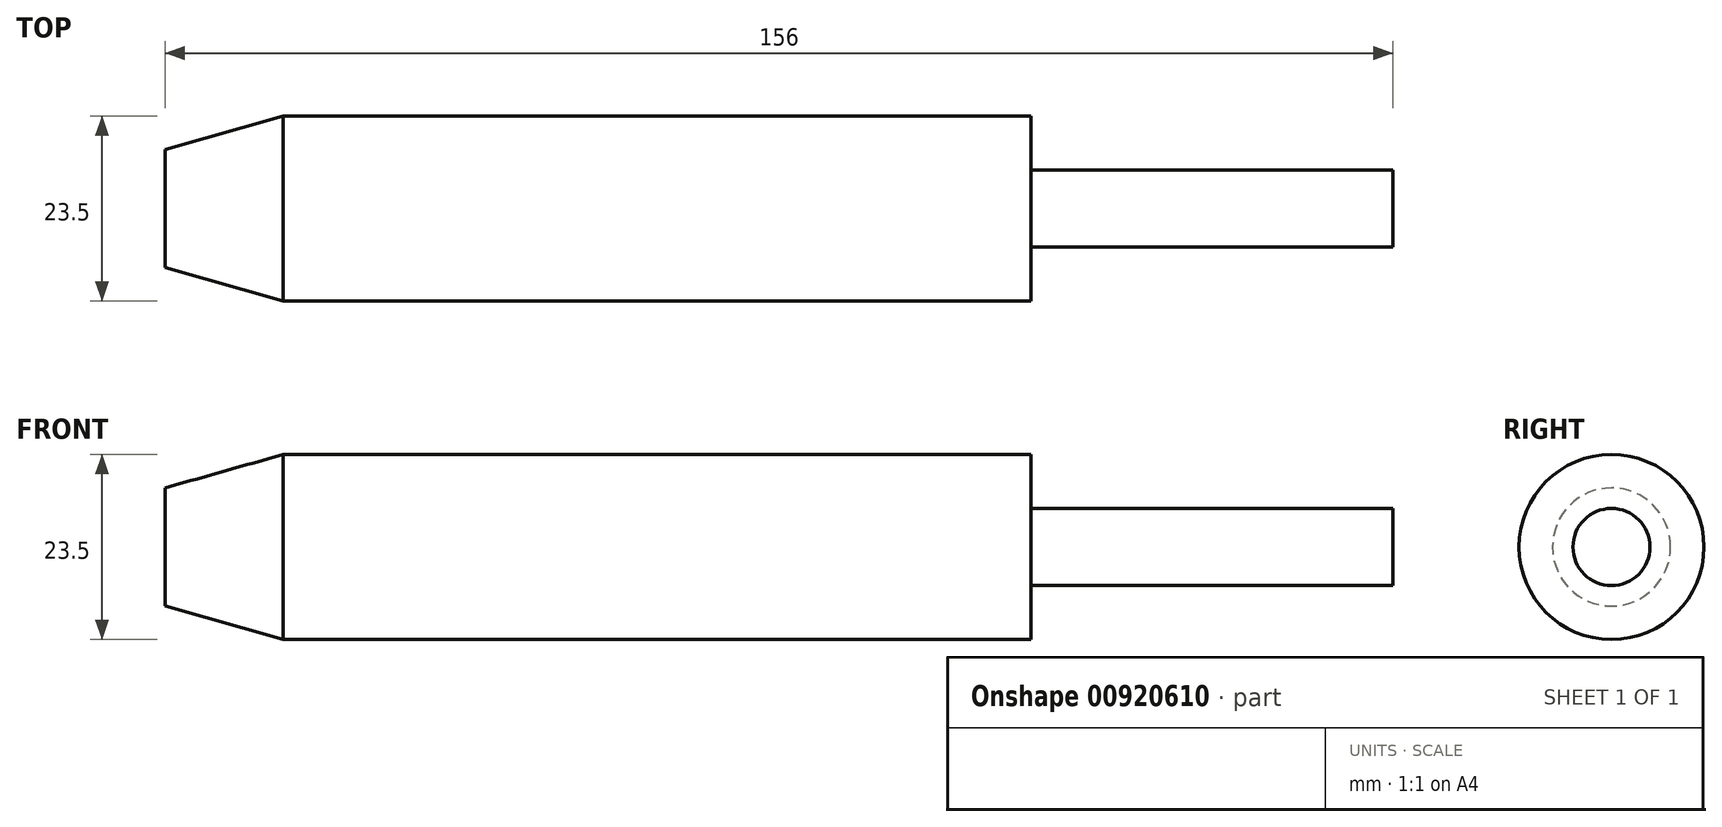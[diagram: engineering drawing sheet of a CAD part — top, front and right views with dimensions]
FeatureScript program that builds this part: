
annotation { "Feature Type Name" : "Feature", "Feature Type Description" : "" }
export const myFeature = defineFeature(function(context is Context, id is Id, definition is map)
    precondition{}
    {
        {
            var Q0;
            Q0=qCreatedBy(makeId("Front.planeOp"),FACE);
            var sketch = newSketch(context, id + "F0", { "sketchPlane" : qUnion([Q0])});
            skLineSegment(sketch, "E0", {"start": v(0, 0) * mm, "end": v(-55.86, 0) * mm, "construction": true});
            skLineSegment(sketch, "E1", {"start": v(46, 0) * mm, "end": v(46, 4.9) * mm});
            skLineSegment(sketch, "E2", {"start": v(46, 4.9) * mm, "end": v(0, 4.9) * mm});
            skLineSegment(sketch, "E3", {"start": v(0, 4.9) * mm, "end": v(0, 11.75) * mm});
            skLineSegment(sketch, "E4", {"start": v(0, 11.75) * mm, "end": v(-95, 11.75) * mm});
            skLineSegment(sketch, "E5", {"start": v(-95, 11.75) * mm, "end": v(-110, 7.5) * mm});
            skLineSegment(sketch, "E6", {"start": v(-110, 7.5) * mm, "end": v(-110, 0) * mm});
            skLineSegment(sketch, "E7", {"start": v(-110, 0) * mm, "end": v(46, 0) * mm});
            skSolve(sketch);
        }
        {
            var Q0;
            Q0=makeQuery(id+"F0.imprint","IMPRINT",FACE,{"disambiguationData":[TD([[makeQuery(id+"F0.imprint","IMPRINT",EDGE,{"derivedFrom":sQuery(id+"F0.wireOp",EDGE,"E1")}),1.0]])]});
            var Q1;
            Q1=sQuery(id+"F0.wireOp",EDGE,"E7");
            revolve(context, id + "F1", {"surfaceOperationType" : NewSurfaceOperationType.NEW, "entities" : qUnion([Q0]), "axis" : qUnion([Q1]), "revolveType" : RevolveType.FULL});
        }
    });
